# Revit family: svetilnik_alfresco_star_k_mini
name_source: partatom
category: Осветительные приборы
revit_build: Autodesk Revit 2016 (Build: 20150506_1715(x64)
units: mm (PartAtom-declared; Revit-internal decimal feet)

## family parameters
Всегда вертикально = Да
Источник света = Да
На основе рабочей плоскости = Нет
Общий = Нет
При загрузке вырезать с полостями = Нет
Размер круглого соединителя = Использовать диаметр
Тип детали = Нормальный
Точка расчета площади = Нет

## types (1)
- STAR-K мини
    ADSK_Артикул = ДТУ481
    ADSK_Единица измерения = шт.
    ADSK_Завод-изготовитель = ALFRESCO
    ADSK_Количество фаз = 2
    ADSK_Количество фаз числовое = 2
    ADSK_Коэффициент мощности = 0.98
    ADSK_Масса = 2
    ADSK_Модель = ДТУ-48-AF STAR-K мини
    ADSK_Наименование = Светодиодный светильник STAR-K мини ДТУ-48-AF-7Вт-0,65
    ADSK_Напряжение = 220 В
    ADSK_Номинальная мощность = 7 Вт
    ADSK_Полная мощность = 7 В·А
    ADSK_Размер_Высота = 650 мм
    ADSK_Размер_Длина = 108 мм
    ADSK_Размер_Ширина = 108 мм
    ADSK_Ток = 0 А
    ADSK_Энергоэффективность = 100 лм/Вт
    IP Class = IP 65
    URL = http://www.allfresco.ru
    Блок аварийного питания = Нет
    Видимая форма излучения при визуализации = Нет
    Высота крышки = 40 мм
    Высота плафона = 524 мм
    Изготовитель = ALFRESCO
    Излучение по длине прямоугольника = 65 мм
    Излучение по ширине прямоугольника = 65 мм
    Класс защиты = 1
    Класс пожароопасности = F (светильники предназначены для установки непосредственно на поверхность из нормально воспламеняемых материалов)
    Климатическая зона = У1
    Корпус светильника = Сталь крашенная чёрная
    Материал рассеивателя = Прозрачное закаленное стекло
    Область использования = ландшафт, коттедж. Посёлки,микрорайоны
    Плафон = Прозрачное закаленное стекло
    Полная установленная мощность = 7 В·А
    Светофильтр = 16777215
    Смещение цветовой температуры при затухании лампы = <Нет>
    Температура эксплуатации = -35 +40
    Тип ИС = LED-светодиоды
    Тип КСС = Круглосимметричная
    Тип ПРА = -
    Тип продукции = LED-светильник
    Угол наклона = 90.00°
    Файл фотометрической сетки = Star-k mini 7W.IES
    Цветовая температура = 2700-6500
    Ширина корпуса = 108 мм
    Ширина фланца = 100 мм

## geometry (parser evidence)
native form markers: Blend x2
no freeform markers — native parametric forms only
